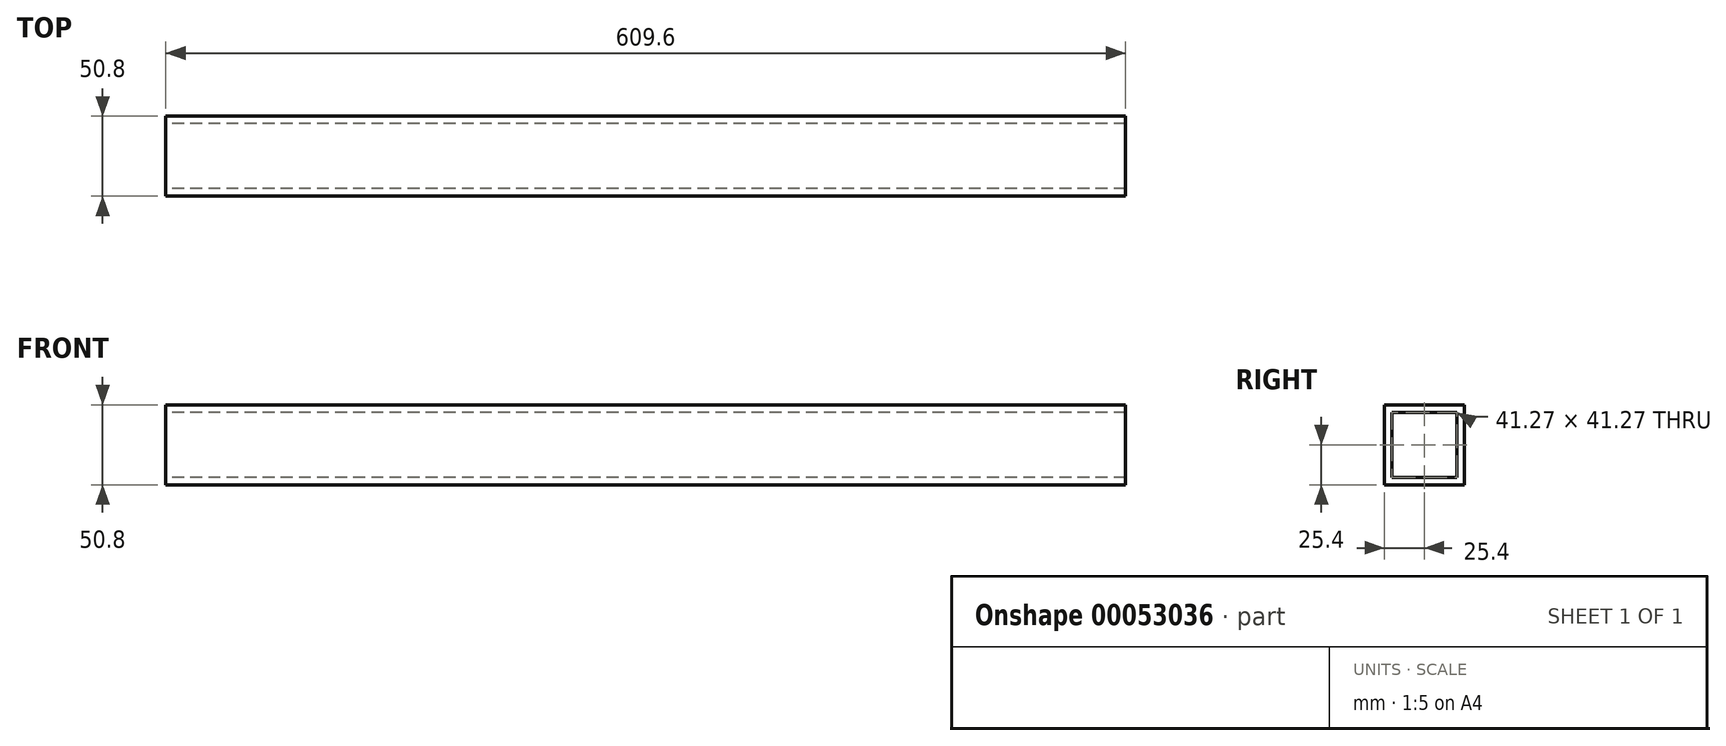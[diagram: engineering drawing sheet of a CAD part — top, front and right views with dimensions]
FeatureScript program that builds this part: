
annotation { "Feature Type Name" : "Feature", "Feature Type Description" : "" }
export const myFeature = defineFeature(function(context is Context, id is Id, definition is map)
    precondition{}
    {
        {
            var Q0;
            Q0=qCreatedBy(makeId("Right.planeOp"),FACE);
            var sketch = newSketch(context, id + "F0", { "sketchPlane" : qUnion([Q0])});
            skLineSegment(sketch, "E0.bottom", {"start": v(0, 0) * mm, "end": v(-50.8, 0) * mm});
            skLineSegment(sketch, "E0.top", {"start": v(0, 50.8) * mm, "end": v(-50.8, 50.8) * mm});
            skLineSegment(sketch, "E0.left", {"start": v(0, 0) * mm, "end": v(0, 50.8) * mm});
            skLineSegment(sketch, "E0.right", {"start": v(-50.8, 0) * mm, "end": v(-50.8, 50.8) * mm});
            skLineSegment(sketch, "E1.bottom", {"start": v(-46.04, 46.04) * mm, "end": v(-4.76, 46.04) * mm});
            skLineSegment(sketch, "E1.top", {"start": v(-46.04, 4.76) * mm, "end": v(-4.76, 4.76) * mm});
            skLineSegment(sketch, "E1.left", {"start": v(-46.04, 46.04) * mm, "end": v(-46.04, 4.76) * mm});
            skLineSegment(sketch, "E1.right", {"start": v(-4.76, 46.04) * mm, "end": v(-4.76, 4.76) * mm});
            skSolve(sketch);
        }
        {
            var Q0;
            Q0=makeQuery(id+"F0.imprint","IMPRINT",FACE,{"disambiguationData":[TD([[makeQuery(id+"F0.imprint","IMPRINT",EDGE,{"derivedFrom":sQuery(id+"F0.wireOp",EDGE,"E0.bottom")}),-1.0]])]});
            extrude(context, id + "F1", {"entities" : qUnion([Q0]), "depth" : 609.6 * mm});
        }
    });
